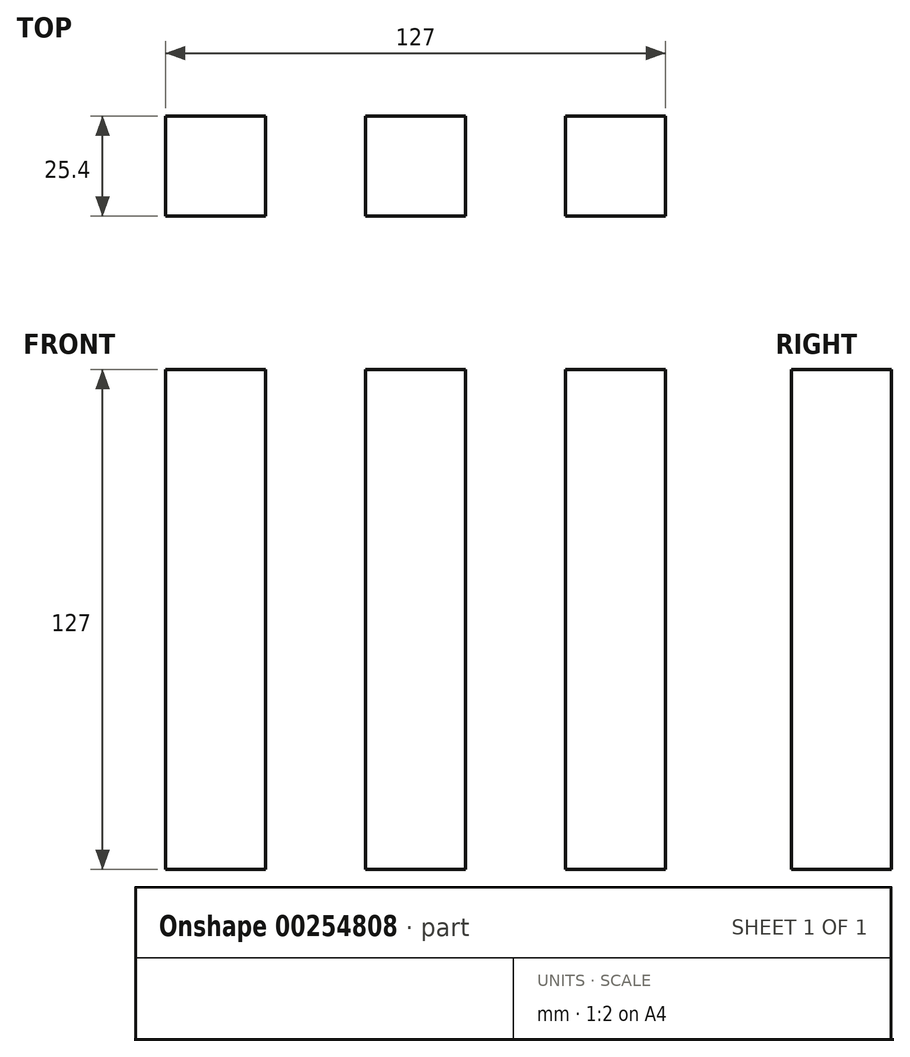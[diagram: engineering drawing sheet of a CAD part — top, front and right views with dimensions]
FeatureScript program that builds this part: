
annotation { "Feature Type Name" : "Feature", "Feature Type Description" : "" }
export const myFeature = defineFeature(function(context is Context, id is Id, definition is map)
    precondition{}
    {
        {
            var Q0;
            Q0=qCreatedBy(makeId("Front.planeOp"),FACE);
            var sketch = newSketch(context, id + "F0", { "sketchPlane" : qUnion([Q0])});
            skLineSegment(sketch, "E0.bottom", {"start": v(-65.95, 139.97) * mm, "end": v(-40.55, 139.97) * mm});
            skLineSegment(sketch, "E0.top", {"start": v(-65.95, 12.97) * mm, "end": v(-40.55, 12.97) * mm});
            skLineSegment(sketch, "E0.left", {"start": v(-65.95, 139.97) * mm, "end": v(-65.95, 12.97) * mm});
            skLineSegment(sketch, "E0.right", {"start": v(-40.55, 139.97) * mm, "end": v(-40.55, 12.97) * mm});
            skPoint(sketch, "E0.middle", {"position": v(-53.25, 76.47) * mm});
            skPoint(sketch, "E1.endSnap0", {"position": v(-40.55, 76.47) * mm});
            skLineSegment(sketch, "E2.bottom", {"start": v(10.25, 139.97) * mm, "end": v(-15.15, 139.97) * mm});
            skLineSegment(sketch, "E2.top", {"start": v(10.25, 12.97) * mm, "end": v(-15.15, 12.97) * mm});
            skLineSegment(sketch, "E2.left", {"start": v(10.25, 139.97) * mm, "end": v(10.25, 12.97) * mm});
            skLineSegment(sketch, "E2.right", {"start": v(-15.15, 139.97) * mm, "end": v(-15.15, 12.97) * mm});
            skPoint(sketch, "E2.middle", {"position": v(-2.45, 76.47) * mm});
            skPoint(sketch, "E3.endSnap0", {"position": v(10.25, 76.47) * mm});
            skLineSegment(sketch, "E4.bottom", {"start": v(35.65, 139.97) * mm, "end": v(61.05, 139.97) * mm});
            skLineSegment(sketch, "E4.top", {"start": v(35.65, 12.97) * mm, "end": v(61.05, 12.97) * mm});
            skLineSegment(sketch, "E4.left", {"start": v(35.65, 139.97) * mm, "end": v(35.65, 12.97) * mm});
            skLineSegment(sketch, "E4.right", {"start": v(61.05, 139.97) * mm, "end": v(61.05, 12.97) * mm});
            skPoint(sketch, "E4.middle", {"position": v(48.35, 76.47) * mm});
            skLineSegment(sketch, "E5", {"start": v(-40.55, 76.47) * mm, "end": v(-40.55, 139.97) * mm});
            skLineSegment(sketch, "E6", {"start": v(10.25, 76.47) * mm, "end": v(10.25, 139.97) * mm});
            skLineSegment(sketch, "E7", {"start": v(61.05, 76.47) * mm, "end": v(61.05, 139.97) * mm});
            skLineSegment(sketch, "E8", {"start": v(-40.55, 76.47) * mm, "end": v(-40.55, 12.97) * mm});
            skSolve(sketch);
        }
        {
            var Q0;
            Q0=makeQuery(id+"F0.imprint","IMPRINT",FACE,{"disambiguationData":[TD([[makeQuery(id+"F0.imprint","IMPRINT",EDGE,{"derivedFrom":sQuery(id+"F0.wireOp",EDGE,"E0.bottom")}),-1.0]])]});
            var Q1;
            Q1=makeQuery(id+"F0.imprint","IMPRINT",FACE,{"disambiguationData":[TD([[makeQuery(id+"F0.imprint","IMPRINT",EDGE,{"derivedFrom":sQuery(id+"F0.wireOp",EDGE,"E2.bottom")}),1.0]])]});
            var Q2;
            Q2=makeQuery(id+"F0.imprint","IMPRINT",FACE,{"disambiguationData":[TD([[makeQuery(id+"F0.imprint","IMPRINT",EDGE,{"derivedFrom":sQuery(id+"F0.wireOp",EDGE,"E4.bottom")}),-1.0]])]});
            extrude(context, id + "F1", {"entities" : qUnion([Q0, Q1, Q2]), "depth" : 25.4 * mm});
        }
    });
